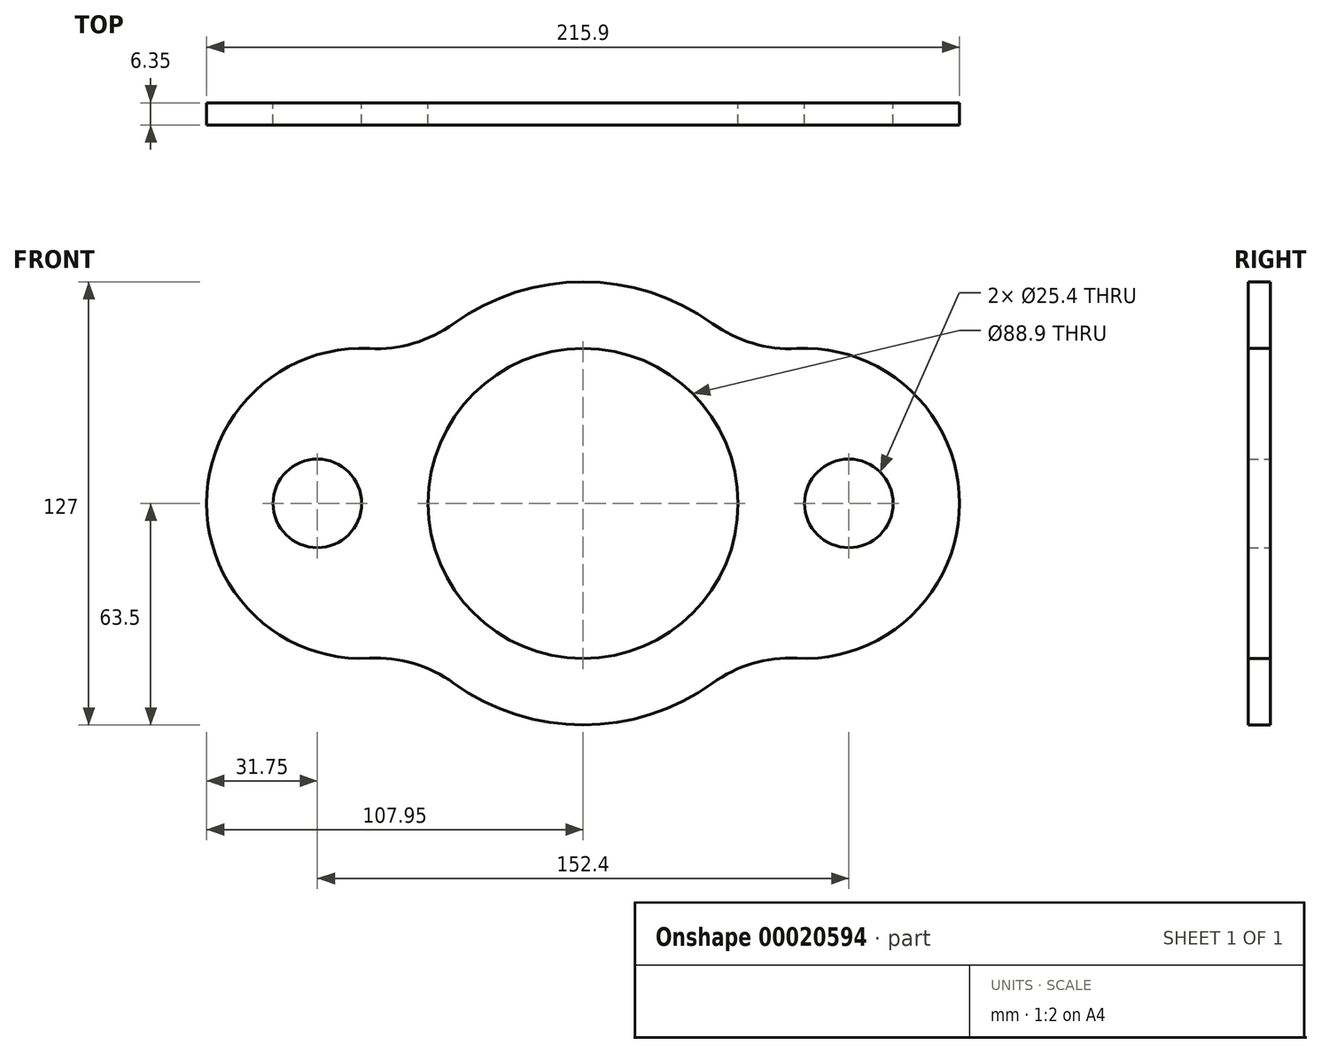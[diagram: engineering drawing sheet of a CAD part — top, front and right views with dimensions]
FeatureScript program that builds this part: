
annotation { "Feature Type Name" : "Feature", "Feature Type Description" : "" }
export const myFeature = defineFeature(function(context is Context, id is Id, definition is map)
    precondition{}
    {
        {
            var Q0;
            Q0=qCreatedBy(makeId("Front.planeOp"),FACE);
            var sketch = newSketch(context, id + "F0", { "sketchPlane" : qUnion([Q0])});
            skCircle(sketch, "E0", {"center": v(0, 0) * mm, "radius": 44.45 * mm});
            skArc(sketch, "E1", {"start": v(-37.1, -51.53) * mm, "mid": v(0, -63.5) * mm, "end": v(37.1, -51.53) * mm});
            skArc(sketch, "E2", {"start": v(-61.28, 44.4) * mm, "mid": v(-107.95, 0) * mm, "end": v(-61.28, -44.4) * mm});
            skArc(sketch, "E3", {"start": v(61.28, -44.4) * mm, "mid": v(107.95, 0) * mm, "end": v(61.28, 44.4) * mm});
            skArc(sketch, "E4.trimOffspring", {"start": v(37.1, 51.53) * mm, "mid": v(0, 63.5) * mm, "end": v(-37.1, 51.53) * mm});
            skPoint(sketch, "E5.visualSharp", {"position": v(47.94, 41.64) * mm});
            skArc(sketch, "E5.filletArc", {"start": v(37.1, 51.53) * mm, "mid": v(48.59, 45.9) * mm, "end": v(61.28, 44.4) * mm});
            skPoint(sketch, "E6.visualSharp", {"position": v(-47.94, 41.64) * mm});
            skArc(sketch, "E6.filletArc", {"start": v(-61.28, 44.4) * mm, "mid": v(-48.59, 45.9) * mm, "end": v(-37.1, 51.53) * mm});
            skPoint(sketch, "E7.visualSharp", {"position": v(-47.94, -41.64) * mm});
            skArc(sketch, "E7.filletArc", {"start": v(-37.1, -51.53) * mm, "mid": v(-48.59, -45.9) * mm, "end": v(-61.28, -44.4) * mm});
            skPoint(sketch, "E8.visualSharp", {"position": v(47.94, -41.64) * mm});
            skArc(sketch, "E8.filletArc", {"start": v(61.28, -44.4) * mm, "mid": v(48.59, -45.9) * mm, "end": v(37.1, -51.53) * mm});
            skLineSegment(sketch, "E9", {"start": v(0, 0) * mm, "end": v(76.2, 0) * mm});
            skLineSegment(sketch, "E10", {"start": v(0, 0) * mm, "end": v(-76.2, 0) * mm});
            skCircle(sketch, "E11", {"center": v(-76.2, 0) * mm, "radius": 12.7 * mm});
            skCircle(sketch, "E12", {"center": v(76.2, 0) * mm, "radius": 12.7 * mm});
            skSolve(sketch);
        }
        {
            var Q0;
            Q0 = qSketchRegion(id + "F0", true);
            extrude(context, id + "F1", {"entities" : qUnion([Q0]), "depth" : 6.35 * mm});
        }
    });
